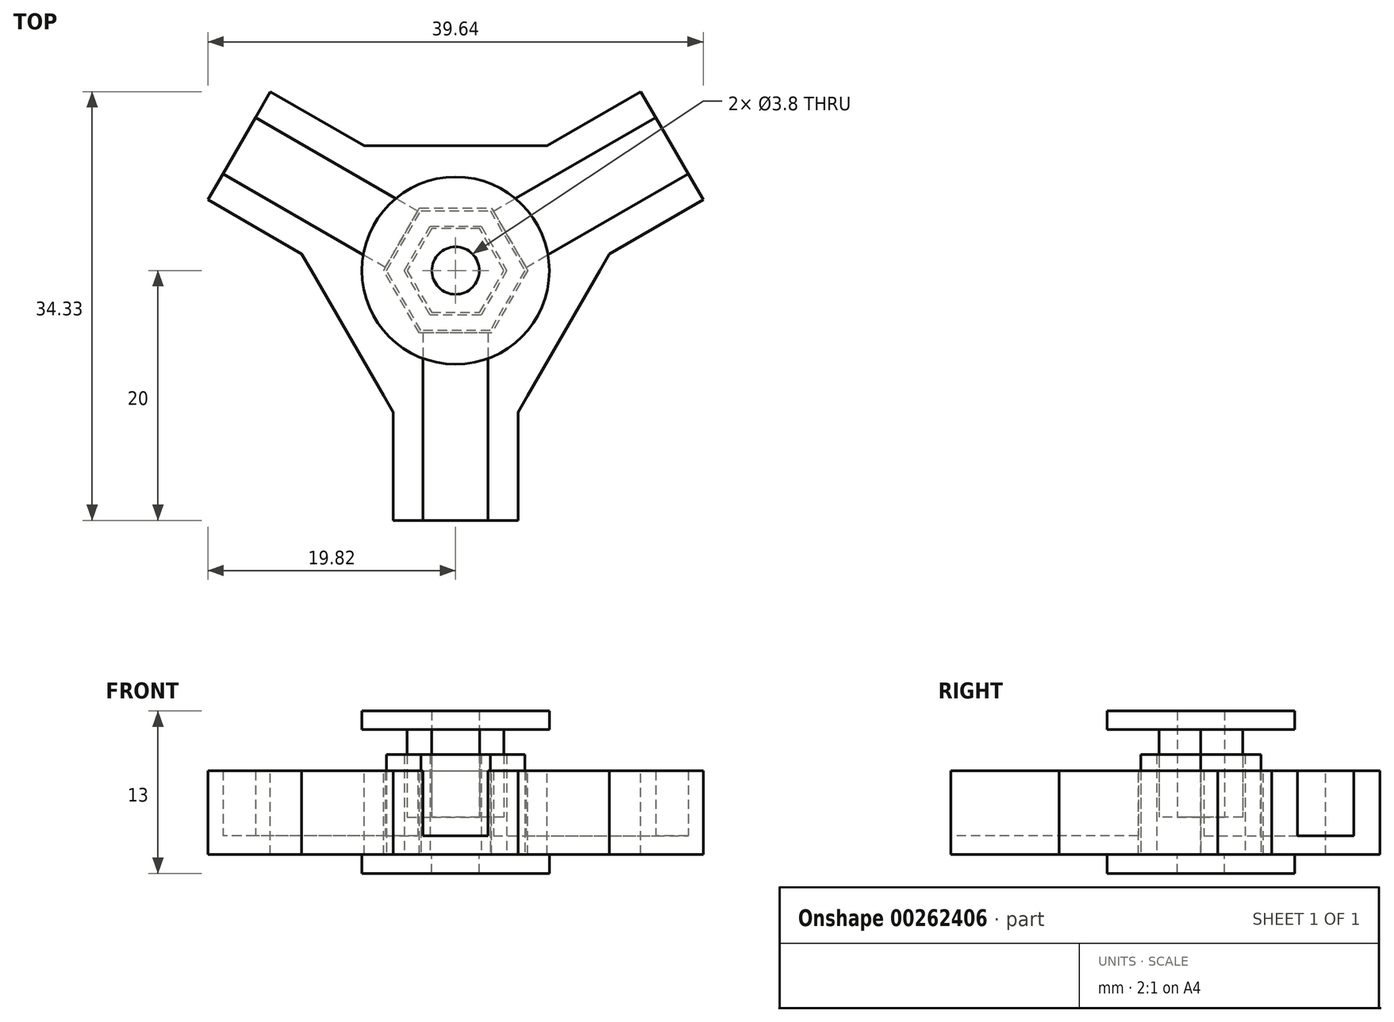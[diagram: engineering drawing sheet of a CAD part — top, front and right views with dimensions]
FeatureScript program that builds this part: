
annotation { "Feature Type Name" : "Feature", "Feature Type Description" : "" }
export const myFeature = defineFeature(function(context is Context, id is Id, definition is map)
    precondition{}
    {
        {
            var Q0;
            Q0=qCreatedBy(makeId("Top.planeOp"),FACE);
            var sketch = newSketch(context, id + "F0", { "sketchPlane" : qUnion([Q0])});
            skCircle(sketch, "E0.cCircle", {"center": v(0, 0) * mm, "radius": 10 * mm, "construction": true});
            skLineSegment(sketch, "E0.0", {"start": v(2.6, -10) * mm, "end": v(-2.6, -10) * mm});
            skLineSegment(sketch, "E0.1", {"start": v(-5.77, -10) * mm, "end": v(-11.55, 0) * mm});
            skLineSegment(sketch, "E0.2", {"start": v(-11.55, 0) * mm, "end": v(-5.77, 10) * mm});
            skLineSegment(sketch, "E0.3", {"start": v(-5.77, 10) * mm, "end": v(5.77, 10) * mm});
            skLineSegment(sketch, "E0.4", {"start": v(5.77, 10) * mm, "end": v(11.55, 0) * mm});
            skLineSegment(sketch, "E0.5", {"start": v(11.55, 0) * mm, "end": v(5.77, -10) * mm});
            skPoint(sketch, "E0.0.midPoint", {"position": v(0, -10) * mm});
            skCircle(sketch, "E1.cCircle", {"center": v(0, 0) * mm, "radius": 5 * mm, "construction": true});
            skLineSegment(sketch, "E1.0", {"start": v(2.89, -5) * mm, "end": v(-2.89, -5) * mm});
            skLineSegment(sketch, "E1.1", {"start": v(-2.89, -5) * mm, "end": v(-5.77, 0) * mm});
            skLineSegment(sketch, "E1.2", {"start": v(-5.77, 0) * mm, "end": v(-2.89, 5) * mm});
            skLineSegment(sketch, "E1.3", {"start": v(-2.89, 5) * mm, "end": v(2.89, 5) * mm});
            skLineSegment(sketch, "E1.4", {"start": v(2.89, 5) * mm, "end": v(5.77, 0) * mm});
            skLineSegment(sketch, "E1.5", {"start": v(5.77, 0) * mm, "end": v(2.89, -5) * mm});
            skPoint(sketch, "E1.0.midPoint", {"position": v(0, -5) * mm});
            skLineSegment(sketch, "E2.top", {"start": v(-2.6, -20) * mm, "end": v(2.6, -20) * mm});
            skLineSegment(sketch, "E2.left", {"start": v(-2.6, -5) * mm, "end": v(-2.6, -20) * mm});
            skLineSegment(sketch, "E2.right", {"start": v(2.6, -5) * mm, "end": v(2.6, -20) * mm});
            skLineSegment(sketch, "E3.top", {"start": v(-5, -20) * mm, "end": v(5, -20) * mm});
            skLineSegment(sketch, "E3.right", {"start": v(5, -11.34) * mm, "end": v(5, -20) * mm});
            skLineSegment(sketch, "E4", {"start": v(-5.77, -10) * mm, "end": v(-5, -11.34) * mm});
            skLineSegment(sketch, "E5.MirrorCS", {"start": v(5.77, -10) * mm, "end": v(5, -11.34) * mm});
            skPoint(sketch, "E6.orphan", {"position": v(-2.6, 0) * mm});
            skPoint(sketch, "E3.bottom.start.orphan", {"position": v(2.6, 0) * mm});
            skPoint(sketch, "E7.orphan", {"position": v(-5, 0) * mm});
            skLineSegment(sketch, "E8.trimOffspring", {"start": v(-5, -11.34) * mm, "end": v(-5, -20) * mm});
            skLineSegment(sketch, "E9", {"start": v(-11.55, 0) * mm, "end": v(-5.77, 0) * mm});
            skLineSegment(sketch, "E10", {"start": v(5.77, 0) * mm, "end": v(11.55, 0) * mm});
            skSolve(sketch);
        }
        {
            var Q0;
            Q0=qCreatedBy(makeId("Right.planeOp"),FACE);
            var sketch = newSketch(context, id + "F1", { "sketchPlane" : qUnion([Q0])});
            skPoint(sketch, "E11.0", {"position": v(-20, 0) * mm});
            skPoint(sketch, "E12.0", {"position": v(-11.34, 0) * mm});
            skPoint(sketch, "E13.0", {"position": v(-5, 0) * mm});
            skPoint(sketch, "E14.0", {"position": v(0, 0) * mm});
            skLineSegment(sketch, "E15.bottom", {"start": v(-20, 0) * mm, "end": v(0, 0) * mm});
            skLineSegment(sketch, "E15.top", {"start": v(-20, -1.5) * mm, "end": v(0, -1.5) * mm});
            skLineSegment(sketch, "E15.left", {"start": v(-20, 0) * mm, "end": v(-20, -1.5) * mm});
            skLineSegment(sketch, "E15.right", {"start": v(0, 0) * mm, "end": v(0, -1.5) * mm});
            skLineSegment(sketch, "E16", {"start": v(0, 0) * mm, "end": v(0, 5.2) * mm});
            skLineSegment(sketch, "E17", {"start": v(0, 5.2) * mm, "end": v(-11.34, 5.2) * mm});
            skLineSegment(sketch, "E18", {"start": v(-11.34, 5.2) * mm, "end": v(-20, 0) * mm});
            skLineSegment(sketch, "E19", {"start": v(0, 24.44) * mm, "end": v(0, -17.26) * mm, "construction": true});
            skSolve(sketch);
        }
        {
            var Q0;
            {var subQ0=sQuery(id+"F0.wireOp",EDGE,"E0.0");Q0=makeQuery(id+"F0.imprint","IMPRINT",FACE,{"disambiguationData":[TD([[makeQuery(id+"F0.imprint","IMPRINT",EDGE,{"derivedFrom":subQ0}),1.0]])]});}
            var Q1;
            {var subQ0=sQuery(id+"F0.wireOp",EDGE,"E0.0");Q1=makeQuery(id+"F0.imprint","IMPRINT",FACE,{"disambiguationData":[TD([[makeQuery(id+"F0.imprint","IMPRINT",EDGE,{"derivedFrom":subQ0}),-1.0]])]});}
            var Q2;
            Q2=makeQuery(id+"F0.imprint","IMPRINT",FACE,{"disambiguationData":[TD([[makeQuery(id+"F0.imprint","IMPRINT",EDGE,{"derivedFrom":sQuery(id+"F0.wireOp",EDGE,"E0.1")}),-1.0]])]});
            var Q3;
            Q3=makeQuery(id+"F0.imprint","IMPRINT",FACE,{"disambiguationData":[TD([[makeQuery(id+"F0.imprint","IMPRINT",EDGE,{"derivedFrom":sQuery(id+"F0.wireOp",EDGE,"E0.5")}),-1.0]])]});
            var Q4;
            Q4=sQuery(id+"F1.wireOp",VERTEX,"E15.right.end");
            extrude(context, id + "F2", {"entities" : qUnion([Q0, Q1, Q2, Q3]), "endBound" : BoundingType.UP_TO_VERTEX, "oppositeDirection" : true, "endBoundEntityVertex" : qUnion([Q4]), "depth" : 1.5 * mm});
        }
        {
            var Q0;
            Q0=makeQuery(id+"F0.imprint","IMPRINT",FACE,{"disambiguationData":[TD([[makeQuery(id+"F0.imprint","IMPRINT",EDGE,{"derivedFrom":sQuery(id+"F0.wireOp",EDGE,"E0.1")}),-1.0]])]});
            var Q1;
            Q1=makeQuery(id+"F0.imprint","IMPRINT",FACE,{"disambiguationData":[TD([[makeQuery(id+"F0.imprint","IMPRINT",EDGE,{"derivedFrom":sQuery(id+"F0.wireOp",EDGE,"E0.5")}),-1.0]])]});
            var Q2;
            Q2=sQuery(id+"F1.wireOp",VERTEX,"E17.start");
            extrude(context, id + "F3", {"entities" : qUnion([Q0, Q1]), "operationType" : NewBodyOperationType.ADD, "endBound" : BoundingType.UP_TO_VERTEX, "endBoundEntityVertex" : qUnion([Q2]), "depth" : 5.2 * mm});
        }
        {
            var Q0;
            Q0=makeQuery(id+"F2.opExtrude","SWEPT_BODY",BODY,{"disambiguationData":[OSD([sQuery(id+"F0.wireOp",EDGE,"E0.1"),sQuery(id+"F0.wireOp",EDGE,"E0.5"),sQuery(id+"F0.wireOp",EDGE,"E1.0"),sQuery(id+"F0.wireOp",EDGE,"E1.1"),sQuery(id+"F0.wireOp",EDGE,"E1.5"),sQuery(id+"F0.wireOp",EDGE,"E3.top"),sQuery(id+"F0.wireOp",EDGE,"E3.right"),sQuery(id+"F0.wireOp",EDGE,"E4"),sQuery(id+"F0.wireOp",EDGE,"E5.MirrorCS"),sQuery(id+"F0.wireOp",EDGE,"E8.trimOffspring"),sQuery(id+"F0.wireOp",EDGE,"E9"),sQuery(id+"F0.wireOp",EDGE,"E10")])]});
            var Q1;
            Q1=sQuery(id+"F1.wireOp",EDGE,"E19");
            circularPattern(context, id + "F4", {"operationType" : NewBodyOperationType.ADD, "entities" : qUnion([Q0]), "axis" : qUnion([Q1]), "angle" : 360 * degree, "instanceCount" : 3, "equalSpace" : true});
        }
        {
            var Q0;
            Q0=qCreatedBy(makeId("Top.planeOp"),FACE);
            var sketch = newSketch(context, id + "F5", { "sketchPlane" : qUnion([Q0])});
            skCircle(sketch, "E20.cCircle", {"center": v(0, 0) * mm, "radius": 4.8 * mm, "construction": true});
            skLineSegment(sketch, "E20.0", {"start": v(2.77, -4.8) * mm, "end": v(-2.77, -4.8) * mm});
            skLineSegment(sketch, "E20.1", {"start": v(-2.77, -4.8) * mm, "end": v(-5.54, 0) * mm});
            skLineSegment(sketch, "E20.2", {"start": v(-5.54, 0) * mm, "end": v(-2.77, 4.8) * mm});
            skLineSegment(sketch, "E20.3", {"start": v(-2.77, 4.8) * mm, "end": v(2.77, 4.8) * mm});
            skLineSegment(sketch, "E20.4", {"start": v(2.77, 4.8) * mm, "end": v(5.54, 0) * mm});
            skLineSegment(sketch, "E20.5", {"start": v(5.54, 0) * mm, "end": v(2.77, -4.8) * mm});
            skPoint(sketch, "E20.0.midPoint", {"position": v(0, -4.8) * mm});
            skCircle(sketch, "E21", {"center": v(0, 0) * mm, "radius": 7.5 * mm});
            skCircle(sketch, "E22", {"center": v(0, 0) * mm, "radius": 1.9 * mm});
            skCircle(sketch, "E23.cCircle", {"center": v(0, 0) * mm, "radius": 3.55 * mm, "construction": true});
            skLineSegment(sketch, "E23.0", {"start": v(2.05, -3.55) * mm, "end": v(-2.05, -3.55) * mm});
            skLineSegment(sketch, "E23.1", {"start": v(-2.05, -3.55) * mm, "end": v(-4.1, 0) * mm});
            skLineSegment(sketch, "E23.2", {"start": v(-4.1, 0) * mm, "end": v(-2.05, 3.55) * mm});
            skLineSegment(sketch, "E23.3", {"start": v(-2.05, 3.55) * mm, "end": v(2.05, 3.55) * mm});
            skLineSegment(sketch, "E23.4", {"start": v(2.05, 3.55) * mm, "end": v(4.1, 0) * mm});
            skLineSegment(sketch, "E23.5", {"start": v(4.1, 0) * mm, "end": v(2.05, -3.55) * mm});
            skPoint(sketch, "E23.0.midPoint", {"position": v(0, -3.55) * mm});
            skCircle(sketch, "E24.cCircle", {"center": v(0, 0) * mm, "radius": 3.35 * mm, "construction": true});
            skLineSegment(sketch, "E24.0", {"start": v(1.93, -3.35) * mm, "end": v(-1.93, -3.35) * mm});
            skLineSegment(sketch, "E24.1", {"start": v(-1.93, -3.35) * mm, "end": v(-3.87, 0) * mm});
            skLineSegment(sketch, "E24.2", {"start": v(-3.87, 0) * mm, "end": v(-1.93, 3.35) * mm});
            skLineSegment(sketch, "E24.3", {"start": v(-1.93, 3.35) * mm, "end": v(1.93, 3.35) * mm});
            skLineSegment(sketch, "E24.4", {"start": v(1.93, 3.35) * mm, "end": v(3.87, 0) * mm});
            skLineSegment(sketch, "E24.5", {"start": v(3.87, 0) * mm, "end": v(1.93, -3.35) * mm});
            skPoint(sketch, "E24.0.midPoint", {"position": v(0, -3.35) * mm});
            skSolve(sketch);
        }
        {
            var Q0;
            Q0=qCreatedBy(makeId("Right.planeOp"),FACE);
            var sketch = newSketch(context, id + "F6", { "sketchPlane" : qUnion([Q0])});
            skPoint(sketch, "E25.0", {"position": v(0, -1.5) * mm});
            skLineSegment(sketch, "E26.bottom", {"start": v(5, -1.5) * mm, "end": v(-5, -1.5) * mm});
            skLineSegment(sketch, "E26.top", {"start": v(5, 1.5) * mm, "end": v(-5, 1.5) * mm});
            skLineSegment(sketch, "E26.left", {"start": v(5, -1.5) * mm, "end": v(5, 1.5) * mm});
            skLineSegment(sketch, "E26.right", {"start": v(-5, -1.5) * mm, "end": v(-5, 1.5) * mm});
            skPoint(sketch, "E26.middle", {"position": v(0, 0) * mm});
            skLineSegment(sketch, "E27.bottom", {"start": v(-6.25, -1.5) * mm, "end": v(6.25, -1.5) * mm});
            skLineSegment(sketch, "E27.top", {"start": v(-6.25, -3) * mm, "end": v(6.25, -3) * mm});
            skLineSegment(sketch, "E27.left", {"start": v(-6.25, -1.5) * mm, "end": v(-6.25, -3) * mm});
            skLineSegment(sketch, "E27.right", {"start": v(6.25, -1.5) * mm, "end": v(6.25, -3) * mm});
            skLineSegment(sketch, "E28.top", {"start": v(5, 6.5) * mm, "end": v(-5, 6.5) * mm});
            skLineSegment(sketch, "E28.left", {"start": v(5, 1.5) * mm, "end": v(5, 6.5) * mm});
            skLineSegment(sketch, "E28.right", {"start": v(-5, 1.5) * mm, "end": v(-5, 6.5) * mm});
            skLineSegment(sketch, "E29.bottom", {"start": v(-5, 6.5) * mm, "end": v(5, 6.5) * mm});
            skLineSegment(sketch, "E29.top", {"start": v(-5, 8.5) * mm, "end": v(5, 8.5) * mm});
            skLineSegment(sketch, "E29.left", {"start": v(-5, 6.5) * mm, "end": v(-5, 8.5) * mm});
            skLineSegment(sketch, "E29.right", {"start": v(5, 6.5) * mm, "end": v(5, 8.5) * mm});
            skLineSegment(sketch, "E30.bottom", {"start": v(-6.25, 8.5) * mm, "end": v(6.25, 8.5) * mm});
            skLineSegment(sketch, "E30.top", {"start": v(-6.25, 10) * mm, "end": v(6.25, 10) * mm});
            skLineSegment(sketch, "E30.left", {"start": v(-6.25, 8.5) * mm, "end": v(-6.25, 10) * mm});
            skLineSegment(sketch, "E30.right", {"start": v(6.25, 8.5) * mm, "end": v(6.25, 10) * mm});
            skSolve(sketch);
        }
        {
            var Q0;
            Q0=makeQuery(id+"F5.imprint","IMPRINT",FACE,{"disambiguationData":[TD([[makeQuery(id+"F5.imprint","IMPRINT",EDGE,{"derivedFrom":sQuery(id+"F5.wireOp",EDGE,"E20.0")}),1.0]])]});
            var Q1;
            Q1=makeQuery(id+"F5.imprint","IMPRINT",FACE,{"disambiguationData":[TD([[makeQuery(id+"F5.imprint","IMPRINT",EDGE,{"derivedFrom":sQuery(id+"F5.wireOp",EDGE,"E20.0")}),-1.0]])]});
            var Q2;
            Q2=makeQuery(id+"F5.imprint","IMPRINT",FACE,{"disambiguationData":[TD([[makeQuery(id+"F5.imprint","IMPRINT",EDGE,{"derivedFrom":sQuery(id+"F5.wireOp",EDGE,"E22")}),-1.0]])]});
            var Q3;
            Q3=makeQuery(id+"F5.imprint","IMPRINT",FACE,{"disambiguationData":[TD([[makeQuery(id+"F5.imprint","IMPRINT",EDGE,{"derivedFrom":sQuery(id+"F5.wireOp",EDGE,"E23.0")}),-1.0]])]});
            var Q4;
            Q4=sQuery(id+"F6.wireOp",VERTEX,"E27.top.start");
            var Q5;
            Q5=sQuery(id+"F6.wireOp",VERTEX,"E27.left.start");
            extrude(context, id + "F7", {"entities" : qUnion([Q0, Q1, Q2, Q3]), "endBound" : BoundingType.UP_TO_VERTEX, "oppositeDirection" : true, "endBoundEntityVertex" : qUnion([Q4]), "depth" : 25 * mm, "hasSecondDirection" : true, "secondDirectionBound" : SecondDirectionBoundingType.UP_TO_VERTEX, "secondDirectionOppositeDirection" : true, "secondDirectionBoundEntityVertex" : qUnion([Q5]), "secondDirectionDepth" : 25 * mm});
        }
        {
            var Q0;
            Q0=makeQuery(id+"F5.imprint","IMPRINT",FACE,{"disambiguationData":[TD([[makeQuery(id+"F5.imprint","IMPRINT",EDGE,{"derivedFrom":sQuery(id+"F5.wireOp",EDGE,"E20.0")}),-1.0]])]});
            var Q1;
            Q1=sQuery(id+"F6.wireOp",VERTEX,"E29.bottom.start");
            var Q2;
            Q2=sQuery(id+"F6.wireOp",VERTEX,"E27.top.start");
            extrude(context, id + "F8", {"entities" : qUnion([Q0]), "operationType" : NewBodyOperationType.ADD, "endBound" : BoundingType.UP_TO_VERTEX, "endBoundEntityVertex" : qUnion([Q1]), "depth" : 25 * mm, "hasSecondDirection" : true, "secondDirectionBound" : SecondDirectionBoundingType.UP_TO_VERTEX, "secondDirectionOppositeDirection" : true, "secondDirectionBoundEntityVertex" : qUnion([Q2]), "secondDirectionDepth" : 25 * mm});
        }
        {
            var Q0;
            Q0=makeQuery(id+"F5.imprint","IMPRINT",FACE,{"disambiguationData":[TD([[makeQuery(id+"F5.imprint","IMPRINT",EDGE,{"derivedFrom":sQuery(id+"F5.wireOp",EDGE,"E20.0")}),1.0]])]});
            var Q1;
            Q1=makeQuery(id+"F5.imprint","IMPRINT",FACE,{"disambiguationData":[TD([[makeQuery(id+"F5.imprint","IMPRINT",EDGE,{"derivedFrom":sQuery(id+"F5.wireOp",EDGE,"E20.0")}),-1.0]])]});
            var Q2;
            Q2=makeQuery(id+"F5.imprint","IMPRINT",FACE,{"disambiguationData":[TD([[makeQuery(id+"F5.imprint","IMPRINT",EDGE,{"derivedFrom":sQuery(id+"F5.wireOp",EDGE,"E22")}),-1.0]])]});
            var Q3;
            Q3=makeQuery(id+"F5.imprint","IMPRINT",FACE,{"disambiguationData":[TD([[makeQuery(id+"F5.imprint","IMPRINT",EDGE,{"derivedFrom":sQuery(id+"F5.wireOp",EDGE,"E23.0")}),-1.0]])]});
            var Q4;
            Q4=sQuery(id+"F6.wireOp",VERTEX,"E30.left.end");
            var Q5;
            Q5=sQuery(id+"F6.wireOp",VERTEX,"E30.bottom.start");
            extrude(context, id + "F9", {"entities" : qUnion([Q0, Q1, Q2, Q3]), "endBound" : BoundingType.UP_TO_VERTEX, "endBoundEntityVertex" : qUnion([Q4]), "depth" : 25 * mm, "hasSecondDirection" : true, "secondDirectionBound" : SecondDirectionBoundingType.UP_TO_VERTEX, "secondDirectionOppositeDirection" : false, "secondDirectionBoundEntityVertex" : qUnion([Q5]), "secondDirectionDepth" : 25 * mm});
        }
        {
            var Q0;
            Q0=makeQuery(id+"F5.imprint","IMPRINT",FACE,{"disambiguationData":[TD([[makeQuery(id+"F5.imprint","IMPRINT",EDGE,{"derivedFrom":sQuery(id+"F5.wireOp",EDGE,"E22")}),-1.0]])]});
            var Q1;
            Q1=sQuery(id+"F6.wireOp",VERTEX,"E30.right.end");
            var Q2;
            Q2=sQuery(id+"F6.wireOp",VERTEX,"E26.top.start");
            extrude(context, id + "F10", {"entities" : qUnion([Q0]), "operationType" : NewBodyOperationType.ADD, "endBound" : BoundingType.UP_TO_VERTEX, "endBoundEntityVertex" : qUnion([Q1]), "depth" : 25 * mm, "hasSecondDirection" : true, "secondDirectionBound" : SecondDirectionBoundingType.UP_TO_VERTEX, "secondDirectionOppositeDirection" : false, "secondDirectionBoundEntityVertex" : qUnion([Q2]), "secondDirectionDepth" : 25 * mm});
        }
    });
